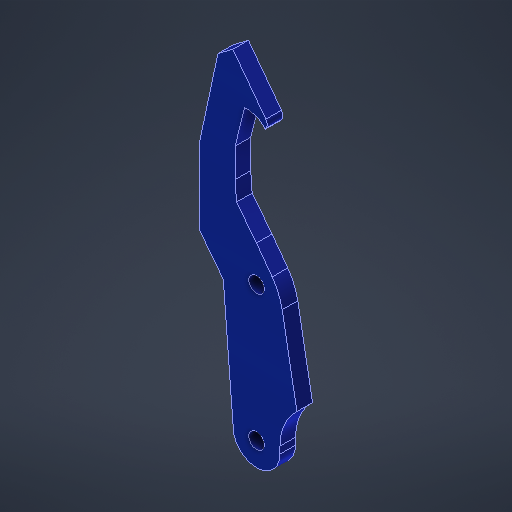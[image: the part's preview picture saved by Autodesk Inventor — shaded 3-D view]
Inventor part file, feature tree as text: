
AUTODESK INVENTOR PART (.ipt)
format: ipt  version: 2025.3 (Build 293356000, 356)  size: 253,440 bytes
history: native  units: in
note: dims shown in document units (in); Inventor stores cm internally (conversion verified against a paired STEP export)
features: fillet x3, extrude x1, sketch x1
ambient origin geometry x8: Origin, YZ Plane, XZ Plane, XY Plane, X Axis, Y Axis, Z Axis, Center Point
bodies: Solid1 (feature_tree)
feature tree (5):
  extrude  "Extrusion1"  Depth=0.1181in
  fillet  "Fillet1"  Radius=1.0236in
  fillet  "Fillet6"  Radius=0.3543in
  fillet  "Fillet7"  Radius=0.3142in
  sketch  "Sketch1"  dims[d0=0.1181in d1=0.1181in d2=1.0236in d3=0.3543in d4=0.3142in d6=0.65in d14=0.1181in d15=0.0in d16=0.3937in d20=0.5906in d34=0.4331in d35=0.0512in]
